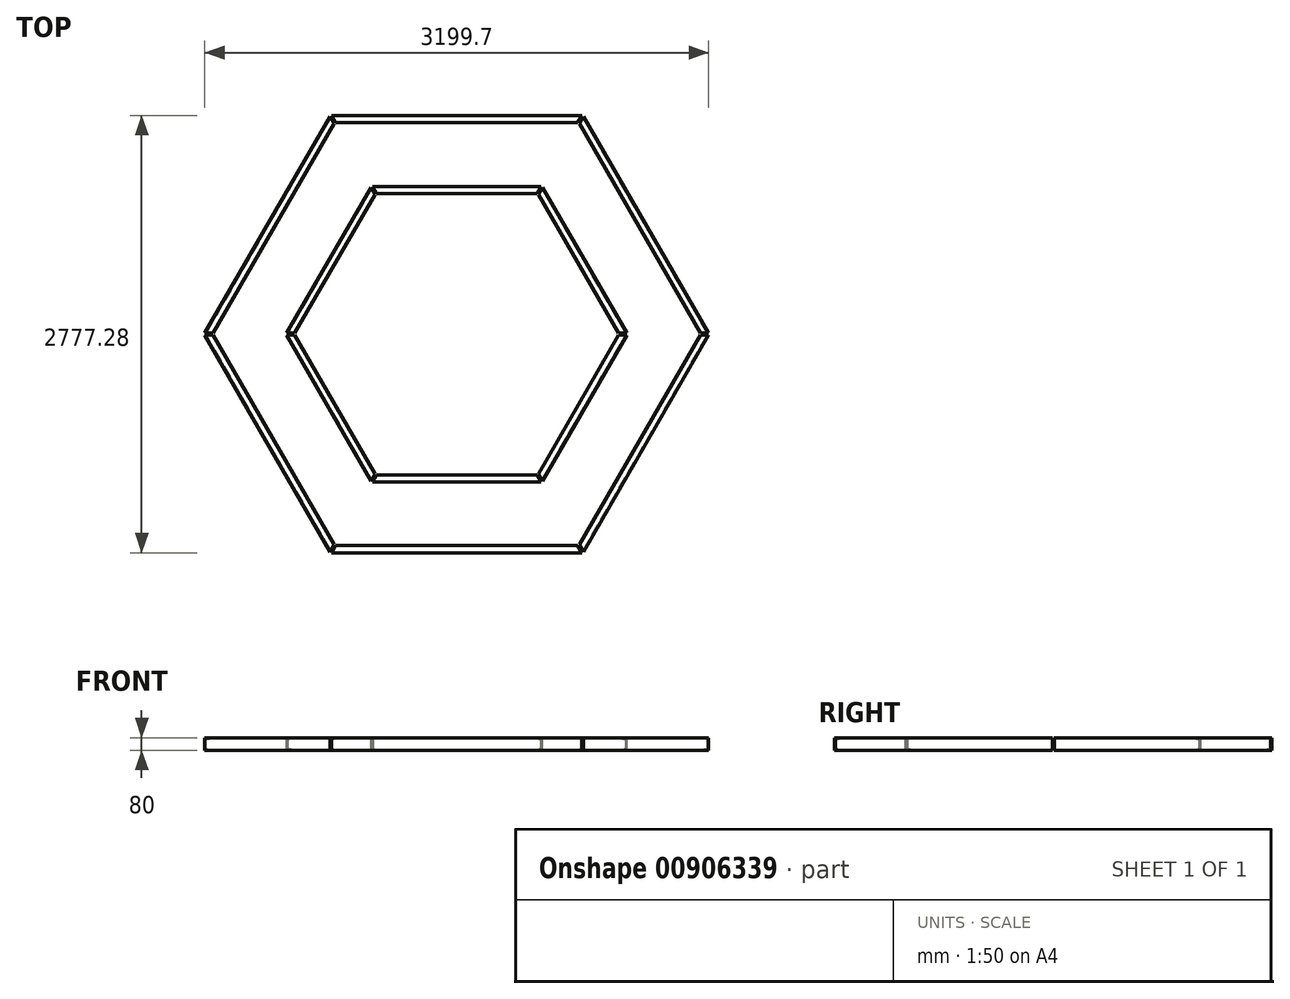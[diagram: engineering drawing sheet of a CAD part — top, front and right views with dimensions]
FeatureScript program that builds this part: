
annotation { "Feature Type Name" : "Feature", "Feature Type Description" : "" }
export const myFeature = defineFeature(function(context is Context, id is Id, definition is map)
    precondition{}
    {
        {
            var Q0;
            Q0=qCreatedBy(makeId("Top.planeOp"),FACE);
            var sketch = newSketch(context, id + "F0", { "sketchPlane" : qUnion([Q0])});
            skArc(sketch, "E0", {"start": v(86.6, -50) * mm, "mid": v(100, 0) * mm, "end": v(86.6, 50) * mm, "construction": true});
            skLineSegment(sketch, "E1", {"start": v(0, 0) * mm, "end": v(1600, 0) * mm, "construction": true});
            skLineSegment(sketch, "E2", {"start": v(1600, 0) * mm, "end": v(1600, -53) * mm});
            skLineSegment(sketch, "E3", {"start": v(1600, -53) * mm, "end": v(91.8, -53) * mm});
            skLineSegment(sketch, "E4.MirrorCS", {"start": v(1600, 0) * mm, "end": v(1600, 53) * mm});
            skLineSegment(sketch, "E5.MirrorCS", {"start": v(1600, 53) * mm, "end": v(91.8, 53) * mm});
            skLineSegment(sketch, "E6.MirrorCS", {"start": v(845.9, 1359.15) * mm, "end": v(91.8, 53) * mm, "construction": true});
            skLineSegment(sketch, "E7.MirrorCS", {"start": v(0, 0) * mm, "end": v(800, 1385.64) * mm, "construction": true});
            skLineSegment(sketch, "E8", {"start": v(91.8, 53) * mm, "end": v(86.6, 50) * mm});
            skLineSegment(sketch, "E9.MirrorCS", {"start": v(91.8, -53) * mm, "end": v(86.6, -50) * mm});
            skLineSegment(sketch, "E10", {"start": v(0, 0) * mm, "end": v(86.6, 50) * mm, "construction": true});
            skArc(sketch, "E11", {"start": v(86.6, -50) * mm, "mid": v(100, 0) * mm, "end": v(86.6, 50) * mm});
            skPoint(sketch, "E12.orphan", {"position": v(84.8, -53) * mm});
            skPoint(sketch, "E13.orphan", {"position": v(84.8, 53) * mm});
            skSolve(sketch);
        }
        {
            var Q0;
            Q0=qCreatedBy(makeId("Top.planeOp"),FACE);
            cPlane(context, id + "F1", {"entities" : qUnion([Q0]), "cplaneType" : CPlaneType.OFFSET, "offset" : 20 * mm, "width" : 150 * mm, "height" : 150 * mm});
        }
        {
            var Q0;
            Q0=qCreatedBy(id+"F1.planeOp",FACE);
            var sketch = newSketch(context, id + "F2", { "sketchPlane" : qUnion([Q0])});
            skCircle(sketch, "E14", {"center": v(0, 0) * mm, "radius": 100 * mm, "construction": true});
            skLineSegment(sketch, "E15", {"start": v(84.8, 53) * mm, "end": v(1600, 53) * mm, "construction": true});
            skLineSegment(sketch, "E16", {"start": v(1600, 53) * mm, "end": v(1600, -53) * mm, "construction": true});
            skLineSegment(sketch, "E17", {"start": v(1600, -53) * mm, "end": v(84.8, -53) * mm, "construction": true});
            skPoint(sketch, "E18.orphan", {"position": v(0, -53) * mm});
            skLineSegment(sketch, "E19.MirrorCS", {"start": v(-1600, 53) * mm, "end": v(-1600, -53) * mm, "construction": true});
            skLineSegment(sketch, "E20.MirrorCS", {"start": v(-84.8, 53) * mm, "end": v(-1600, 53) * mm, "construction": true});
            skLineSegment(sketch, "E21.MirrorCS", {"start": v(-1600, -53) * mm, "end": v(-84.8, -53) * mm, "construction": true});
            skLineSegment(sketch, "E22", {"start": v(0, 0) * mm, "end": v(1112.42, 642.26) * mm, "construction": true});
            skLineSegment(sketch, "E23.MirrorCS", {"start": v(845.9, 1359.14) * mm, "end": v(754.1, 1412.14) * mm, "construction": true});
            skLineSegment(sketch, "E24.MirrorCS", {"start": v(754.1, 1412.14) * mm, "end": v(-3.5, 99.94) * mm, "construction": true});
            skLineSegment(sketch, "E25.MirrorCS", {"start": v(88.3, 46.94) * mm, "end": v(845.9, 1359.14) * mm, "construction": true});
            skLineSegment(sketch, "E26.MirrorCS", {"start": v(-88.3, 46.94) * mm, "end": v(-845.9, 1359.14) * mm, "construction": true});
            skLineSegment(sketch, "E27.MirrorCS", {"start": v(-754.1, 1412.14) * mm, "end": v(3.5, 99.94) * mm, "construction": true});
            skLineSegment(sketch, "E28.MirrorCS", {"start": v(-845.9, 1359.14) * mm, "end": v(-754.1, 1412.14) * mm, "construction": true});
            skLineSegment(sketch, "E29.MirrorCS", {"start": v(-845.9, -1359.14) * mm, "end": v(-754.1, -1412.14) * mm, "construction": true});
            skLineSegment(sketch, "E30.MirrorCS", {"start": v(-88.3, -46.94) * mm, "end": v(-845.9, -1359.14) * mm, "construction": true});
            skLineSegment(sketch, "E31.MirrorCS", {"start": v(-754.1, -1412.14) * mm, "end": v(3.5, -99.94) * mm, "construction": true});
            skLineSegment(sketch, "E32.MirrorCS", {"start": v(754.1, -1412.14) * mm, "end": v(-3.5, -99.94) * mm, "construction": true});
            skLineSegment(sketch, "E33.MirrorCS", {"start": v(88.3, -46.94) * mm, "end": v(845.9, -1359.14) * mm, "construction": true});
            skLineSegment(sketch, "E34.MirrorCS", {"start": v(845.9, -1359.14) * mm, "end": v(754.1, -1412.14) * mm, "construction": true});
            skLineSegment(sketch, "E35", {"start": v(1600, 0) * mm, "end": v(1600, -6) * mm, "construction": true});
            skLineSegment(sketch, "E36", {"start": v(1600, -6) * mm, "end": v(124.94, -6) * mm, "construction": true});
            skLineSegment(sketch, "E37", {"start": v(800, -1385.64) * mm, "end": v(0, 0) * mm, "construction": true});
            skLineSegment(sketch, "E38", {"start": v(156.54, -259.14) * mm, "end": v(805.2, -1382.64) * mm, "construction": true});
            skLineSegment(sketch, "E39", {"start": v(805.2, -1382.64) * mm, "end": v(1600, -6) * mm, "construction": true});
            skLineSegment(sketch, "E40", {"start": v(779.22, -1337.64) * mm, "end": v(1548.04, -6) * mm, "construction": true});
            skLineSegment(sketch, "E41", {"start": v(0, 0) * mm, "end": v(1202.6, -694.32) * mm, "construction": true});
            skLineSegment(sketch, "E42", {"start": v(1080.4, -6) * mm, "end": v(812.9, -469.32) * mm, "construction": true});
            skSolve(sketch);
        }
        {
            var Q0;
            Q0=qCreatedBy(makeId("Front.planeOp"),FACE);
            var sketch = newSketch(context, id + "F3", { "sketchPlane" : qUnion([Q0])});
            skLineSegment(sketch, "E43", {"start": v(0, 0) * mm, "end": v(0, 330.86) * mm, "construction": true});
            skSolve(sketch);
        }
        {
            var Q0;
            Q0=sQuery(id+"F2.wireOp",EDGE,"E39");
            cPoint(context, id + "F4", {"entities" : qUnion([Q0]), "parameter" : 0.5});
        }
        {
            var Q0;
            Q0=sQuery(id+"F3.wireOp",VERTEX,"E43.end");
            var Q1;
            Q1 = qCreatedBy(id + "F4" ,VERTEX);
            var Q2;
            Q2=sQuery(id+"F0.wireOp",VERTEX,"E1.start");
            cPlane(context, id + "F5", {"entities" : qUnion([Q0, Q1, Q2]), "cplaneType" : CPlaneType.THREE_POINT, "offset" : 25 * mm, "width" : 150 * mm, "height" : 150 * mm});
        }
        {
            var Q0;
            Q0=qCreatedBy(id+"F5.planeOp",FACE);
            var sketch = newSketch(context, id + "F6", { "sketchPlane" : qUnion([Q0])});
            skLineSegment(sketch, "E44", {"start": v(1388.64, 20) * mm, "end": v(1388.64, 100) * mm});
            skLineSegment(sketch, "E45", {"start": v(1388.64, 100) * mm, "end": v(1343.64, 100) * mm});
            skLineSegment(sketch, "E46", {"start": v(1388.64, 20) * mm, "end": v(1343.64, 20) * mm});
            skArc(sketch, "E47", {"start": v(1343.64, 100) * mm, "mid": v(1344.57, 97.43) * mm, "end": v(1346.94, 96.06) * mm});
            skLineSegment(sketch, "E48", {"start": v(1382.64, 83) * mm, "end": v(1382.64, 37) * mm});
            skLineSegment(sketch, "E49", {"start": v(1382.64, 60) * mm, "end": v(1388.64, 60) * mm, "construction": true});
            skArc(sketch, "E50", {"start": v(1382.64, 83) * mm, "mid": v(1380.77, 88.14) * mm, "end": v(1376.04, 90.88) * mm});
            skArc(sketch, "E51", {"start": v(1376.04, 29.12) * mm, "mid": v(1380.77, 31.86) * mm, "end": v(1382.64, 37) * mm});
            skArc(sketch, "E52", {"start": v(1346.94, 23.94) * mm, "mid": v(1344.57, 22.57) * mm, "end": v(1343.64, 20) * mm});
            skLineSegment(sketch, "E53", {"start": v(1346.94, 96.06) * mm, "end": v(1376.04, 90.88) * mm});
            skLineSegment(sketch, "E54", {"start": v(1346.94, 23.94) * mm, "end": v(1376.04, 29.12) * mm});
            skSolve(sketch);
        }
        {
            var Q0;
            Q0 = qSketchRegion(id + "F6", true);
            extrude(context, id + "F7", {"entities" : qUnion([Q0]), "endBound" : BoundingType.SYMMETRIC, "depth" : 1589 * mm, "offsetDistance" : 25 * mm});
        }
        {
            var Q0;
            Q0=makeQuery(id+"F7.opExtrude","SWEPT_FACE",FACE,{"disambiguationData":[OSD([sQuery(id+"F6.wireOp",EDGE,"E45")])]});
            var sketch = newSketch(context, id + "F8", { "sketchPlane" : qUnion([Q0])});
            skLineSegment(sketch, "E55", {"start": v(805.35, -1382.38) * mm, "end": v(779.37, -1337.38) * mm});
            skLineSegment(sketch, "E56", {"start": v(779.37, -1337.38) * mm, "end": v(766.38, -1359.88) * mm});
            skLineSegment(sketch, "E57", {"start": v(766.38, -1359.88) * mm, "end": v(805.35, -1382.38) * mm});
            skLineSegment(sketch, "E58.MirrorCS", {"start": v(1547.89, -6.26) * mm, "end": v(1560.88, 16.24) * mm});
            skLineSegment(sketch, "E59.MirrorCS", {"start": v(1599.85, -6.26) * mm, "end": v(1547.89, -6.26) * mm});
            skLineSegment(sketch, "E60.MirrorCS", {"start": v(1560.88, 16.24) * mm, "end": v(1599.85, -6.26) * mm});
            skSolve(sketch);
        }
        {
            var Q0;
            Q0=makeQuery(id+"F8.imprint","IMPRINT",FACE,{"disambiguationData":[TD([[makeQuery(id+"F8.imprint","IMPRINT",EDGE,{"derivedFrom":sQuery(id+"F8.wireOp",EDGE,"E55")}),1.0]])]});
            var Q1;
            Q1=makeQuery(id+"F8.imprint","IMPRINT",FACE,{"disambiguationData":[TD([[makeQuery(id+"F8.imprint","IMPRINT",EDGE,{"derivedFrom":sQuery(id+"F8.wireOp",EDGE,"E58.MirrorCS")}),-1.0]])]});
            var Q2;
            Q2=makeQuery(id+"F7.opExtrude","SWEPT_FACE",FACE,{"disambiguationData":[OSD([sQuery(id+"F6.wireOp",EDGE,"E46")])]});
            extrude(context, id + "F9", {"entities" : qUnion([Q0, Q1]), "operationType" : NewBodyOperationType.REMOVE, "endBound" : BoundingType.UP_TO_SURFACE, "oppositeDirection" : true, "depth" : 25 * mm, "endBoundEntityFace" : qUnion([Q2]), "offsetDistance" : 25 * mm});
        }
        {
            var Q0;
            Q0=qCreatedBy(id+"F5.planeOp",FACE);
            var sketch = newSketch(context, id + "F10", { "sketchPlane" : qUnion([Q0])});
            skLineSegment(sketch, "E61", {"start": v(938.65, 20) * mm, "end": v(938.65, 100) * mm});
            skLineSegment(sketch, "E62", {"start": v(938.65, 100) * mm, "end": v(893.65, 100) * mm});
            skLineSegment(sketch, "E63", {"start": v(938.65, 20) * mm, "end": v(893.65, 20) * mm});
            skArc(sketch, "E64", {"start": v(932.65, 83) * mm, "mid": v(930.78, 88.14) * mm, "end": v(926.05, 90.88) * mm});
            skArc(sketch, "E65", {"start": v(926.07, 29.13) * mm, "mid": v(930.79, 31.87) * mm, "end": v(932.65, 37) * mm});
            skLineSegment(sketch, "E66", {"start": v(924.65, 83) * mm, "end": v(924.65, 37) * mm, "construction": true});
            skLineSegment(sketch, "E67", {"start": v(932.65, 83) * mm, "end": v(932.65, 37) * mm});
            skLineSegment(sketch, "E68", {"start": v(924.65, 60) * mm, "end": v(938.65, 60) * mm, "construction": true});
            skArc(sketch, "E69", {"start": v(893.65, 100) * mm, "mid": v(894.58, 97.43) * mm, "end": v(896.95, 96.06) * mm});
            skArc(sketch, "E70", {"start": v(897.65, 24) * mm, "mid": v(894.82, 22.83) * mm, "end": v(893.65, 20) * mm});
            skLineSegment(sketch, "E71", {"start": v(896.95, 96.06) * mm, "end": v(926.05, 90.88) * mm});
            skLineSegment(sketch, "E72", {"start": v(897.65, 24) * mm, "end": v(926.07, 29.13) * mm});
            skSolve(sketch);
        }
        {
            var Q0;
            Q0=makeQuery(id+"F10.imprint","IMPRINT",FACE,{"disambiguationData":[TD([[makeQuery(id+"F10.imprint","IMPRINT",EDGE,{"derivedFrom":sQuery(id+"F10.wireOp",EDGE,"E61")}),1.0]])]});
            extrude(context, id + "F11", {"entities" : qUnion([Q0]), "endBound" : BoundingType.SYMMETRIC, "depth" : 1070 * mm, "offsetDistance" : 25 * mm});
        }
        {
            var Q0;
            Q0=makeQuery(id+"F11.opExtrude","SWEPT_FACE",FACE,{"disambiguationData":[OSD([sQuery(id+"F10.wireOp",EDGE,"E62")])]});
            var sketch = newSketch(context, id + "F12", { "sketchPlane" : qUnion([Q0])});
            skLineSegment(sketch, "E73", {"start": v(519.41, -887.65) * mm, "end": v(545.4, -932.65) * mm});
            skLineSegment(sketch, "E74", {"start": v(545.4, -932.65) * mm, "end": v(506.42, -910.15) * mm});
            skLineSegment(sketch, "E75", {"start": v(506.42, -910.15) * mm, "end": v(519.41, -887.65) * mm});
            skLineSegment(sketch, "E76.MirrorCS", {"start": v(1028.43, -6) * mm, "end": v(1080.4, -6) * mm});
            skLineSegment(sketch, "E77.MirrorCS", {"start": v(1041.42, 16.5) * mm, "end": v(1028.43, -6) * mm});
            skLineSegment(sketch, "E78.MirrorCS", {"start": v(1080.4, -6) * mm, "end": v(1041.42, 16.5) * mm});
            skSolve(sketch);
        }
        {
            var Q0;
            Q0 = qSketchRegion(id + "F12", true);
            var Q1;
            Q1=makeQuery(id+"F11.opExtrude","SWEPT_FACE",FACE,{"disambiguationData":[OSD([sQuery(id+"F10.wireOp",EDGE,"E63")])]});
            extrude(context, id + "F13", {"entities" : qUnion([Q0]), "operationType" : NewBodyOperationType.REMOVE, "endBound" : BoundingType.UP_TO_SURFACE, "oppositeDirection" : true, "depth" : 25 * mm, "endBoundEntityFace" : qUnion([Q1]), "offsetDistance" : 25 * mm});
        }
        {
            var Q0;
            Q0=makeQuery(id+"F7.opExtrude","SWEPT_BODY",BODY,{"disambiguationData":[OSD([sQuery(id+"F6.wireOp",EDGE,"E44"),sQuery(id+"F6.wireOp",EDGE,"E45"),sQuery(id+"F6.wireOp",EDGE,"E46"),sQuery(id+"F6.wireOp",EDGE,"E47"),sQuery(id+"F6.wireOp",EDGE,"E48"),sQuery(id+"F6.wireOp",EDGE,"E50"),sQuery(id+"F6.wireOp",EDGE,"E51"),sQuery(id+"F6.wireOp",EDGE,"E52"),sQuery(id+"F6.wireOp",EDGE,"E53"),sQuery(id+"F6.wireOp",EDGE,"E54")])]});
            var Q1;
            Q1=makeQuery(id+"F11.opExtrude","SWEPT_BODY",BODY,{"disambiguationData":[OSD([sQuery(id+"F10.wireOp",EDGE,"E61"),sQuery(id+"F10.wireOp",EDGE,"E62"),sQuery(id+"F10.wireOp",EDGE,"E63"),sQuery(id+"F10.wireOp",EDGE,"E64"),sQuery(id+"F10.wireOp",EDGE,"E65"),sQuery(id+"F10.wireOp",EDGE,"E67"),sQuery(id+"F10.wireOp",EDGE,"E69"),sQuery(id+"F10.wireOp",EDGE,"E70"),sQuery(id+"F10.wireOp",EDGE,"E71"),sQuery(id+"F10.wireOp",EDGE,"E72")])]});
            var Q2;
            Q2=sQuery(id+"F3.wireOp",EDGE,"E43");
            circularPattern(context, id + "F14", {"entities" : qUnion([Q0, Q1]), "axis" : qUnion([Q2]), "angle" : 360 * degree, "instanceCount" : 6, "equalSpace" : true});
        }
    });
